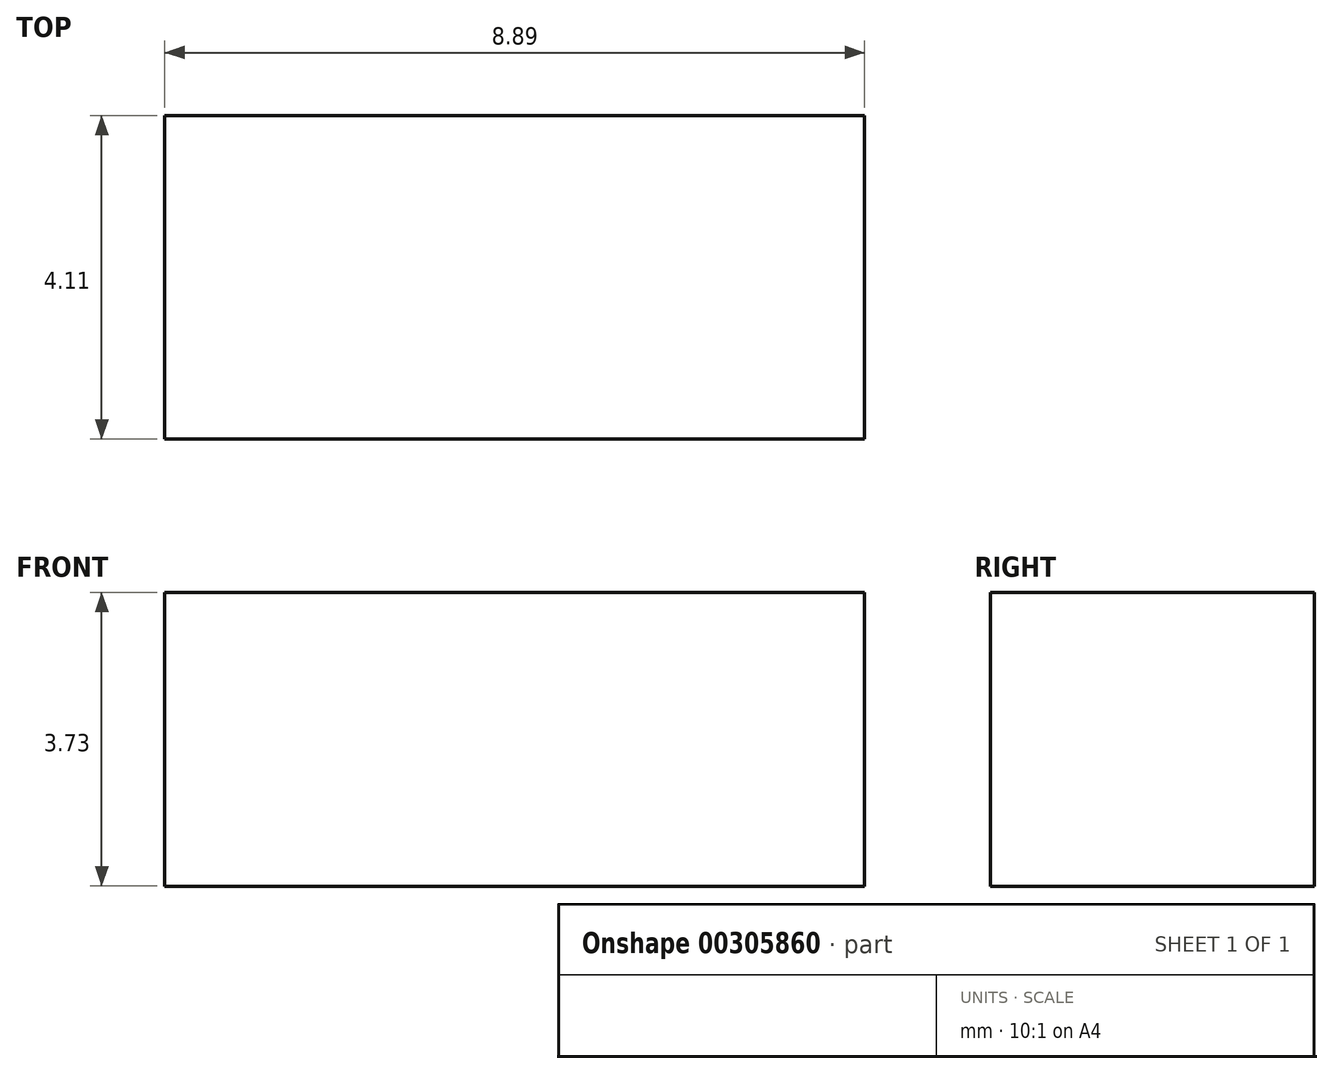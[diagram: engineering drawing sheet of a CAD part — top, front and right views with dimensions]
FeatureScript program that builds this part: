
annotation { "Feature Type Name" : "Feature", "Feature Type Description" : "" }
export const myFeature = defineFeature(function(context is Context, id is Id, definition is map)
    precondition{}
    {
        {
            var Q0;
            Q0=qCreatedBy(makeId("Right.planeOp"),FACE);
            var sketch = newSketch(context, id + "F0", { "sketchPlane" : qUnion([Q0])});
            skLineSegment(sketch, "E0.bottom", {"start": v(-2.98, 6.04) * mm, "end": v(-7.1, 6.04) * mm});
            skLineSegment(sketch, "E0.top", {"start": v(-2.98, 2.3) * mm, "end": v(-7.1, 2.3) * mm});
            skLineSegment(sketch, "E0.left", {"start": v(-2.98, 6.04) * mm, "end": v(-2.98, 2.3) * mm});
            skLineSegment(sketch, "E0.right", {"start": v(-7.1, 6.04) * mm, "end": v(-7.1, 2.3) * mm});
            skSolve(sketch);
        }
        {
            var Q0;
            Q0 = qSketchRegion(id + "F0", true);
            extrude(context, id + "F1", {"entities" : qUnion([Q0]), "depth" : 8.9 * mm});
        }
    });
